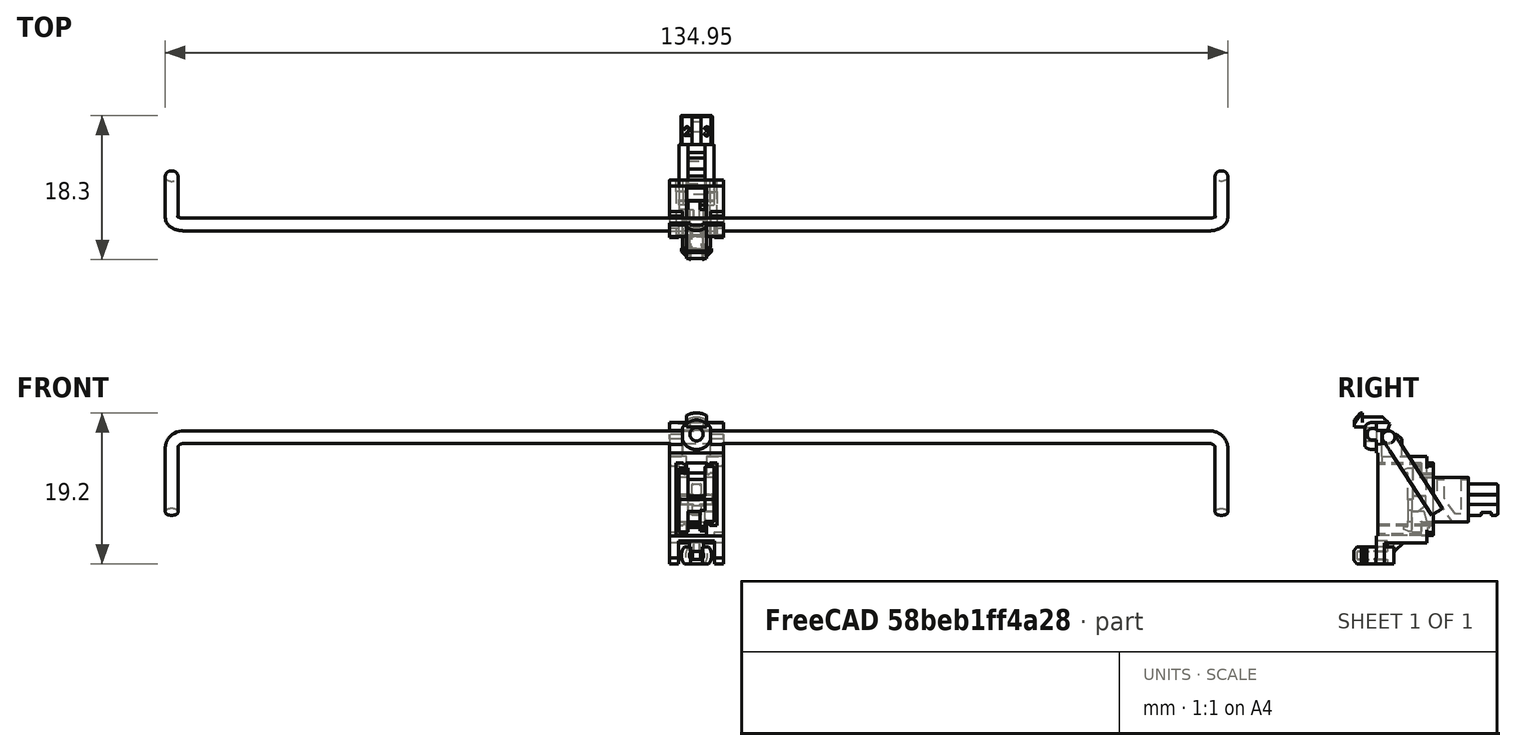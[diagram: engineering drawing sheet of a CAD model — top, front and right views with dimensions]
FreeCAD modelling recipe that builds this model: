
FCSTD DOCUMENT  (FreeCAD 0.18R16158 (Git))
Label: Stabilizer_Cherry_MX_8u
License: CreativeCommons Attribution-ShareAlike
LicenseURL: http://creativecommons.org/licenses/by-sa/4.0/
objects: Part::Feature×4, App::Part×3, PartDesign::Plane×2, Sketcher::SketchObject×2, PartDesign::AdditivePipe×1, PartDesign::Body×1
note: 11 computed .brp shape members not serialized (recipe doc carries the construction recipe); baked Part::Feature solids carry a one-line shape summary decoded from their .brp

FEATURE [Part::Feature] Part__Feature  label="Stabilizer_Base"
  shape: bbox 6.802 x 10.1 x 19.67 mm, 163 faces (baked)
FEATURE [Part::Feature] Part__Feature001  label="Stabilizer_Key"
  Placement = pos=(0,8.1,0) rot=(0,0,1;0rad)
  shape: bbox 4.6 x 11.96 x 8.302 mm, 299 faces (baked)
FEATURE [App::Part] Part  label="Stabilizer_End_1"
  Group = -> [Part__Feature001,Part__Feature]
  Origin = -> Origin001
  Placement = pos=(-66.67,0,0) rot=(0,0,1;0rad)
FEATURE [PartDesign::Plane] DatumPlane
  Length = 147.156
  MapMode = 13
  Placement = pos=(23.0333,0.289849,4.3056) rot=(1,0,0;2.14498rad)
  ResizeMode = 0
  Width = 39.8734
FEATURE [PartDesign::Plane] DatumPlane001
  Length = 39.8734
  MapMode = 11
  Placement = pos=(8e-15,4.09188,-1.57187) rot=(0.272451,-0.272451,0.92279;1.65106rad)
  ResizeMode = 0
  Width = 147.156
FEATURE [Sketcher::SketchObject] Sketch
  MapMode = 5
  Placement = pos=(8e-15,4.09188,-1.57187) rot=(0.272451,-0.272451,0.92279;1.65106rad)
  Support = -> [DatumPlane001]
  sketch-geometry (5):
    g0: Circle CenterX=0 CenterY=66.675 CenterZ=0 NormalX=0 NormalY=0 NormalZ=1 AngleXU=0 Radius=0.8
    g1: Circle [constr] CenterX=0 CenterY=-66.675 CenterZ=0 NormalX=0 NormalY=0 NormalZ=1 AngleXU=0 Radius=0.8
    g2: LineSegment [constr] StartX=0 StartY=66.675 StartZ=0 EndX=0 EndY=0 EndZ=0
    g3: LineSegment [constr] StartX=0 StartY=0 StartZ=0 EndX=0 EndY=-66.675 EndZ=0
    g4: GeomPoint X=0 Y=-66.675 Z=0
  constraints (11):
    c: Diameter(g0) = 1.6
    c: PointOnObject(g0,g-2)
    c: PointOnObject(g1,g-2)
    c: Coincident(g2,g0)
    c: Coincident(g2,g-1)
    c: Coincident(g3,g-1)
    c: Coincident(g3,g1)
    c: Equal(g3,g2)
    c: Distance(g2) = 66.675
    c: Equal(g1,g0)
    c: Coincident(g4,g1)
FEATURE [Sketcher::SketchObject] Sketch001
  ExternalGeometry = -> [Sketch]
  MapMode = 5
  Placement = pos=(23.0333,0.289849,4.3056) rot=(1,0,0;2.14498rad)
  Support = -> [DatumPlane]
  sketch-geometry (5):
    g0: LineSegment StartX=-88.9083 StartY=-7 StartZ=0 EndX=-88.9083 EndY=2.73 EndZ=0
    g1: LineSegment StartX=-88.1083 StartY=3.53 StartZ=0 EndX=42.0417 EndY=3.53 EndZ=0
    g2: LineSegment StartX=42.8417 StartY=2.73 StartZ=0 EndX=42.8417 EndY=-7 EndZ=0
    g3: ArcOfCircle CenterX=-88.1083 CenterY=2.73 CenterZ=0 NormalX=0 NormalY=0 NormalZ=1 AngleXU=0 Radius=0.8 StartAngle=1.5708 EndAngle=3.14159
    g4: ArcOfCircle CenterX=42.0417 CenterY=2.73 CenterZ=0 NormalX=0 NormalY=0 NormalZ=1 AngleXU=0 Radius=0.8 StartAngle=0 EndAngle=1.5708
FEATURE [PartDesign::AdditivePipe] AdditivePipe
  AuxilleryCurvelinear = true
  AuxillerySpineTangent = false
  Binormal = (0,0,0)
  Mode = 0
  Placement = pos=(8e-15,4.09188,-1.57187) rot=(0.272451,-0.272451,0.92279;1.65106rad)
  Profile = -> Sketch
  Spine = -> Sketch001
  SpineTangent = false
  Transformation = 0
  Transition = 0
FEATURE [PartDesign::Body] Body  label="Bar"
  Group = -> [DatumPlane,DatumPlane001,Sketch,Sketch001,AdditivePipe]
  Origin = -> Origin002
  Tip = -> AdditivePipe
FEATURE [Part::Feature] Part__Feature002  label="Stabilizer_Key_"
  Placement = pos=(0,8.1,0) rot=(0,0,1;0rad)
  shape: bbox 4.6 x 11.96 x 8.302 mm, 299 faces (baked)
FEATURE [Part::Feature] Part__Feature003  label="Stabilizer_Base_"
  shape: bbox 6.802 x 10.1 x 19.67 mm, 163 faces (baked)
FEATURE [App::Part] Part001  label="Stabilizer_End_2"
  Group = -> [Part__Feature002,Part__Feature003]
  Origin = -> Origin003
  Placement = pos=(66.665,0,0) rot=(0,0,1;0rad)
FEATURE [App::Part] Stabilizer___open  label="Stabilizer_Cherry_MX_8u"
  Group = -> [Body,Part001,Part]
  Origin = -> Origin
  Placement = pos=(0,8e-16,3.65) rot=(1,0,0;1.5708rad)
